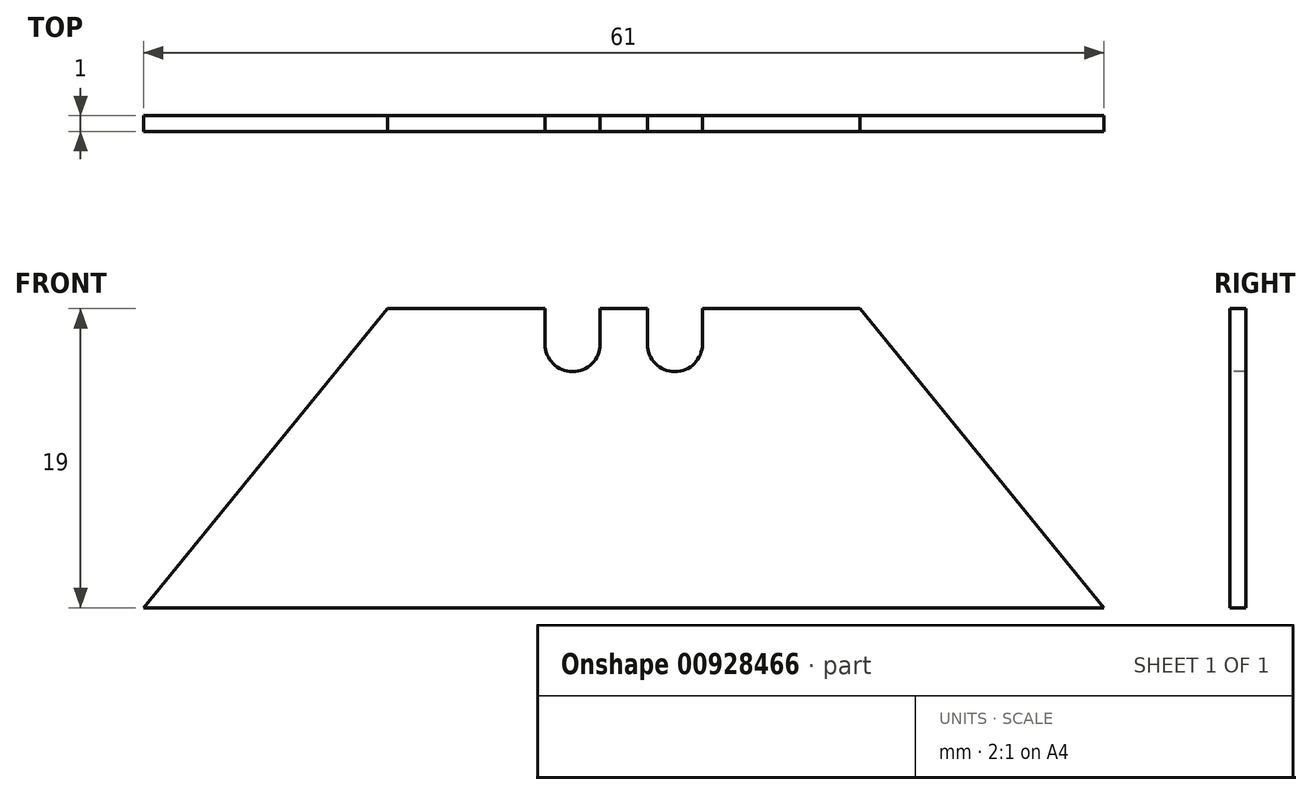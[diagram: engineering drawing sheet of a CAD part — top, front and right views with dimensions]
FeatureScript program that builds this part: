
annotation { "Feature Type Name" : "Feature", "Feature Type Description" : "" }
export const myFeature = defineFeature(function(context is Context, id is Id, definition is map)
    precondition{}
    {
        {
            var Q0;
            Q0=qCreatedBy(makeId("Front.planeOp"),FACE);
            var sketch = newSketch(context, id + "F0", { "sketchPlane" : qUnion([Q0])});
            skLineSegment(sketch, "E0", {"start": v(0, 0) * mm, "end": v(61, 0) * mm});
            skLineSegment(sketch, "E1", {"start": v(30.5, 0) * mm, "end": v(30.5, 19) * mm});
            skLineSegment(sketch, "E2", {"start": v(30.5, 19) * mm, "end": v(45.5, 19) * mm});
            skLineSegment(sketch, "E3", {"start": v(30.5, 19) * mm, "end": v(15.5, 19) * mm});
            skLineSegment(sketch, "E4", {"start": v(15.5, 19) * mm, "end": v(0, 0) * mm});
            skLineSegment(sketch, "E5", {"start": v(45.5, 19) * mm, "end": v(61, 0) * mm});
            skSolve(sketch);
        }
        {
            var Q0;
            {var subQ2=sQuery(id+"F0.wireOp",EDGE,"E1");Q0=makeQuery(id+"F0.imprint","IMPRINT",FACE,{"disambiguationData":[TD([[makeQuery(id+"F0.imprint","IMPRINT",EDGE,{"derivedFrom":subQ2}),1.0]])]});}
            var Q1;
            {var subQ2=sQuery(id+"F0.wireOp",EDGE,"E1");Q1=makeQuery(id+"F0.imprint","IMPRINT",FACE,{"disambiguationData":[TD([[makeQuery(id+"F0.imprint","IMPRINT",EDGE,{"derivedFrom":subQ2}),-1.0]])]});}
            extrude(context, id + "F1", {"entities" : qUnion([Q0, Q1]), "depth" : 1 * mm, "offsetDistance" : 25 * mm});
        }
        {
            var Q0;
            Q0=makeQuery(id+"F1.opExtrude","CAP_FACE",FACE,{"disambiguationData":[OSD([sQuery(id+"F0.wireOp",EDGE,"E0"),sQuery(id+"F0.wireOp",EDGE,"E2"),sQuery(id+"F0.wireOp",EDGE,"E3"),sQuery(id+"F0.wireOp",EDGE,"E4"),sQuery(id+"F0.wireOp",EDGE,"E5")])],"isStart":false});
            var sketch = newSketch(context, id + "F2", { "sketchPlane" : qUnion([Q0])});
            skPoint(sketch, "E6", {"position": v(33.75, 19) * mm});
            skPoint(sketch, "E7", {"position": v(30.5, 19) * mm});
            skPoint(sketch, "E8", {"position": v(27.25, 19) * mm});
            skLineSegment(sketch, "E9", {"start": v(30.5, 19) * mm, "end": v(32, 19) * mm});
            skLineSegment(sketch, "E10", {"start": v(32, 19) * mm, "end": v(32, 16.75) * mm});
            skLineSegment(sketch, "E11", {"start": v(30.5, 19) * mm, "end": v(29, 19) * mm});
            skLineSegment(sketch, "E12", {"start": v(29, 19) * mm, "end": v(29, 16.75) * mm});
            skPoint(sketch, "E13", {"position": v(33.75, 16.75) * mm});
            skPoint(sketch, "E14", {"position": v(27.25, 16.75) * mm});
            skCircle(sketch, "E15", {"center": v(33.75, 16.75) * mm, "radius": 1.75 * mm});
            skCircle(sketch, "E16", {"center": v(27.25, 16.75) * mm, "radius": 1.75 * mm});
            skPoint(sketch, "E17", {"position": v(35.5, 19) * mm});
            skPoint(sketch, "E18", {"position": v(25.5, 19) * mm});
            skLineSegment(sketch, "E19", {"start": v(25.5, 19) * mm, "end": v(25.5, 16.75) * mm});
            skLineSegment(sketch, "E20", {"start": v(35.5, 19) * mm, "end": v(35.5, 16.75) * mm});
            skSolve(sketch);
        }
        {
            var Q0;
            {var subQ0=sQuery(id+"F2.wireOp",EDGE,"E16");var subQ1=makeQuery(id+"F2.imprint","INTERSECT",VERTEX,{"derivedFrom":[sQuery(id+"F2.wireOp",EDGE,"E12"),subQ0]});Q0=makeQuery(id+"F2.imprint","IMPRINT",FACE,{"disambiguationData":[TD([[makeQuery(id+"F2.imprint","IMPRINT",EDGE,{"disambiguationData":[TD([[subQ1,-1.0]])],"derivedFrom":subQ0}),1.0]])]});}
            var Q1;
            {var subQ0=sQuery(id+"F2.wireOp",EDGE,"E15");var subQ1=makeQuery(id+"F2.imprint","INTERSECT",VERTEX,{"derivedFrom":[sQuery(id+"F2.wireOp",EDGE,"E10"),subQ0]});Q1=makeQuery(id+"F2.imprint","IMPRINT",FACE,{"disambiguationData":[TD([[makeQuery(id+"F2.imprint","IMPRINT",EDGE,{"disambiguationData":[TD([[subQ1,1.0]])],"derivedFrom":subQ0}),1.0]])]});}
            var Q2;
            {var subQ0=sQuery(id+"F2.wireOp",EDGE,"E10");Q2=makeQuery(id+"F2.imprint","IMPRINT",FACE,{"disambiguationData":[TD([[makeQuery(id+"F2.imprint","IMPRINT",EDGE,{"derivedFrom":subQ0}),1.0]])]});}
            var Q3;
            {var subQ0=sQuery(id+"F2.wireOp",EDGE,"E12");Q3=makeQuery(id+"F2.imprint","IMPRINT",FACE,{"disambiguationData":[TD([[makeQuery(id+"F2.imprint","IMPRINT",EDGE,{"derivedFrom":subQ0}),-1.0]])]});}
            extrude(context, id + "F3", {"entities" : qUnion([Q0, Q1, Q2, Q3]), "operationType" : NewBodyOperationType.REMOVE, "oppositeDirection" : true, "depth" : 25 * mm, "offsetDistance" : 25 * mm});
        }
    });
